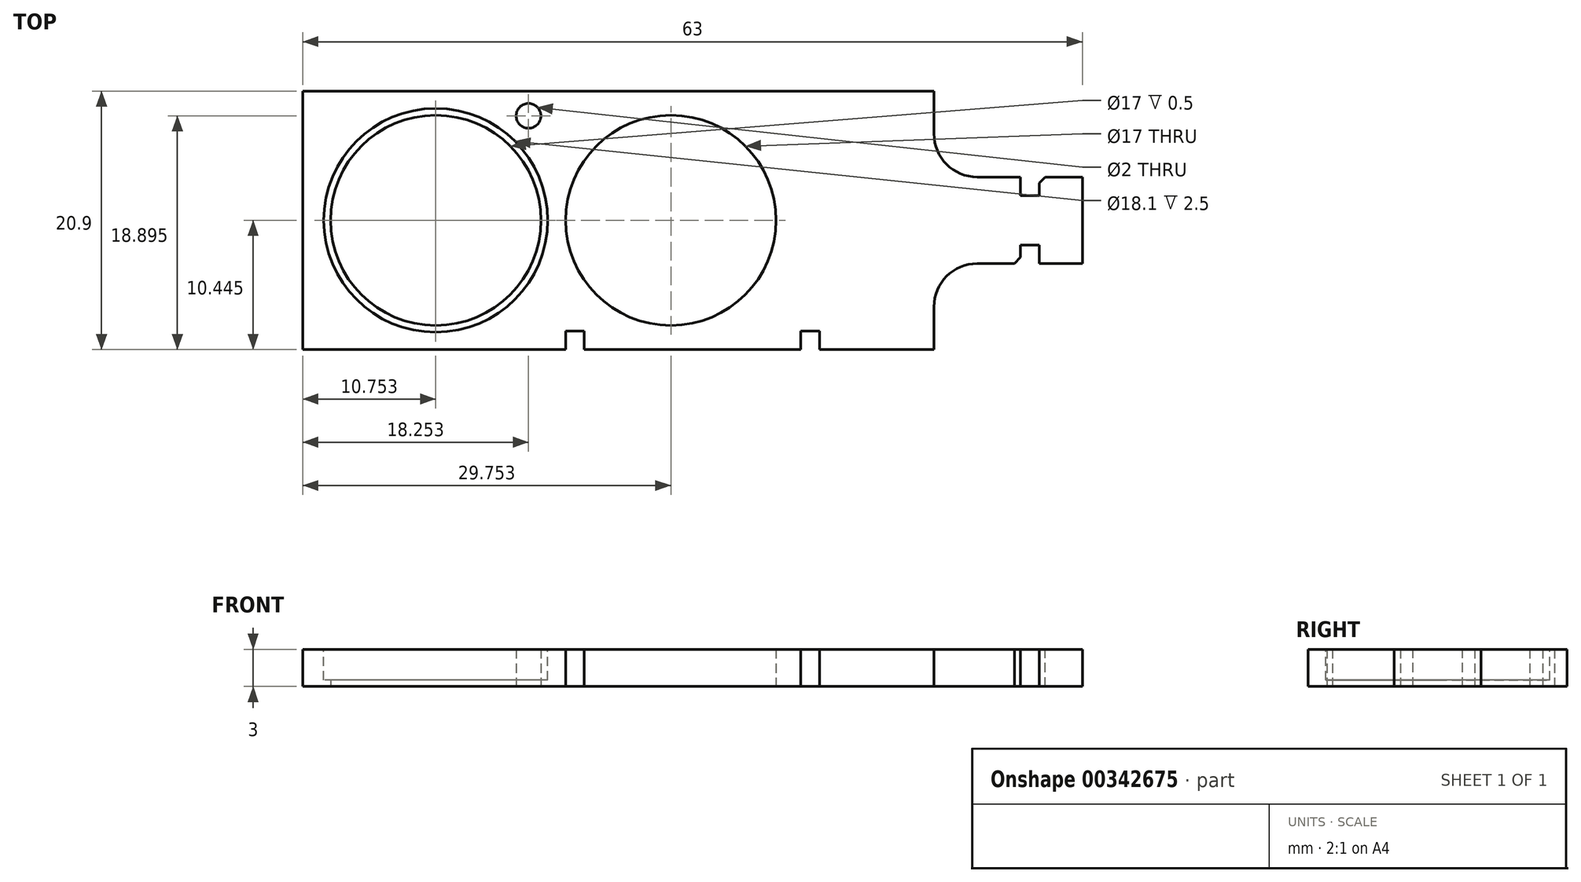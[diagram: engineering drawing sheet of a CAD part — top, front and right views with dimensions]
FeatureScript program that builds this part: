
annotation { "Feature Type Name" : "Feature", "Feature Type Description" : "" }
export const myFeature = defineFeature(function(context is Context, id is Id, definition is map)
    precondition{}
    {
        {
            var Q0;
            Q0=qCreatedBy(makeId("Top.planeOp"),FACE);
            var sketch = newSketch(context, id + "F0", { "sketchPlane" : qUnion([Q0])});
            skLineSegment(sketch, "E0", {"start": v(-30.6, 13.17) * mm, "end": v(20.4, 13.17) * mm});
            skLineSegment(sketch, "E1", {"start": v(20.4, 13.17) * mm, "end": v(20.4, 9.72) * mm});
            skLineSegment(sketch, "E2", {"start": v(23.9, 6.22) * mm, "end": v(32.4, 6.22) * mm});
            skLineSegment(sketch, "E3", {"start": v(32.4, 6.22) * mm, "end": v(32.4, -0.78) * mm});
            skLineSegment(sketch, "E4", {"start": v(32.4, -0.78) * mm, "end": v(23.9, -0.78) * mm});
            skLineSegment(sketch, "E5", {"start": v(20.4, -4.28) * mm, "end": v(20.4, -7.73) * mm});
            skLineSegment(sketch, "E6", {"start": v(-30.6, -7.73) * mm, "end": v(-30.6, 13.17) * mm});
            skPoint(sketch, "E7.orphan", {"position": v(-29.62, 13.17) * mm});
            skPoint(sketch, "E8.visualSharp", {"position": v(20.4, -0.78) * mm});
            skArc(sketch, "E8.filletArc", {"start": v(23.9, -0.78) * mm, "mid": v(21.42, -1.81) * mm, "end": v(20.4, -4.28) * mm});
            skPoint(sketch, "E9.visualSharp", {"position": v(20.4, 6.22) * mm});
            skArc(sketch, "E9.filletArc", {"start": v(20.4, 9.72) * mm, "mid": v(21.42, 7.24) * mm, "end": v(23.9, 6.22) * mm});
            skCircle(sketch, "E10", {"center": v(-19.86, 2.72) * mm, "radius": 8.5 * mm});
            skCircle(sketch, "E11", {"center": v(-0.86, 2.72) * mm, "radius": 8.5 * mm});
            skCircle(sketch, "E12", {"center": v(-12.36, 11.17) * mm, "radius": 1 * mm});
            skLineSegment(sketch, "E13.bottom", {"start": v(-9.36, -6.23) * mm, "end": v(-7.86, -6.23) * mm});
            skLineSegment(sketch, "E13.left", {"start": v(-9.36, -6.23) * mm, "end": v(-9.36, -7.73) * mm});
            skLineSegment(sketch, "E13.right", {"start": v(-7.86, -6.23) * mm, "end": v(-7.86, -7.73) * mm});
            skLineSegment(sketch, "E14.bottom", {"start": v(9.64, -6.23) * mm, "end": v(11.14, -6.23) * mm});
            skLineSegment(sketch, "E14.left", {"start": v(9.64, -6.23) * mm, "end": v(9.64, -7.73) * mm});
            skLineSegment(sketch, "E14.right", {"start": v(11.14, -6.23) * mm, "end": v(11.14, -7.73) * mm});
            skPoint(sketch, "E15", {"position": v(-8.6, -6.23) * mm});
            skPoint(sketch, "E16", {"position": v(10.4, -6.23) * mm});
            skLineSegment(sketch, "E17.trimOffspring", {"start": v(-9.36, -7.73) * mm, "end": v(-30.6, -7.73) * mm});
            skLineSegment(sketch, "E18.trimOffspring", {"start": v(9.64, -7.73) * mm, "end": v(-7.86, -7.73) * mm});
            skLineSegment(sketch, "E19", {"start": v(11.14, -7.73) * mm, "end": v(20.4, -7.73) * mm});
            skSolve(sketch);
        }
        {
            var Q0;
            Q0=qSketchRegion(id+"F0",true);
            extrude(context, id + "F1", {"entities" : qUnion([Q0]), "depth" : 3 * mm});
        }
        {
            var Q0;
            Q0=makeQuery(id+"F1.opExtrude","CAP_FACE",FACE,{"disambiguationData":[OSD([sQuery(id+"F0.wireOp",EDGE,"E0"),sQuery(id+"F0.wireOp",EDGE,"E1"),sQuery(id+"F0.wireOp",EDGE,"E2"),sQuery(id+"F0.wireOp",EDGE,"E3"),sQuery(id+"F0.wireOp",EDGE,"E4"),sQuery(id+"F0.wireOp",EDGE,"E5"),sQuery(id+"F0.wireOp",EDGE,"E6"),sQuery(id+"F0.wireOp",EDGE,"E8.filletArc"),sQuery(id+"F0.wireOp",EDGE,"E9.filletArc"),sQuery(id+"F0.wireOp",EDGE,"E10"),sQuery(id+"F0.wireOp",EDGE,"E11"),sQuery(id+"F0.wireOp",EDGE,"E12"),sQuery(id+"F0.wireOp",EDGE,"E13.bottom"),sQuery(id+"F0.wireOp",EDGE,"E13.left"),sQuery(id+"F0.wireOp",EDGE,"E13.right"),sQuery(id+"F0.wireOp",EDGE,"E14.bottom"),sQuery(id+"F0.wireOp",EDGE,"E14.left"),sQuery(id+"F0.wireOp",EDGE,"E14.right"),sQuery(id+"F0.wireOp",EDGE,"E17.trimOffspring"),sQuery(id+"F0.wireOp",EDGE,"E18.trimOffspring"),sQuery(id+"F0.wireOp",EDGE,"E19")])],"isStart":false});
            var sketch = newSketch(context, id + "F2", { "sketchPlane" : qUnion([Q0])});
            skCircle(sketch, "E20", {"center": v(-19.86, 2.72) * mm, "radius": 9.05 * mm});
            skSolve(sketch);
        }
        {
            var Q0;
            Q0=qSketchRegion(id+"F2",true);
            extrude(context, id + "F3", {"entities" : qUnion([Q0]), "operationType" : NewBodyOperationType.REMOVE, "oppositeDirection" : true, "depth" : 2.5 * mm});
        }
        {
            var Q0;
            Q0=makeQuery(id+"F1.opExtrude","CAP_FACE",FACE,{"disambiguationData":[OSD([sQuery(id+"F0.wireOp",EDGE,"E0"),sQuery(id+"F0.wireOp",EDGE,"E1"),sQuery(id+"F0.wireOp",EDGE,"E2"),sQuery(id+"F0.wireOp",EDGE,"E3"),sQuery(id+"F0.wireOp",EDGE,"E4"),sQuery(id+"F0.wireOp",EDGE,"E5"),sQuery(id+"F0.wireOp",EDGE,"E6"),sQuery(id+"F0.wireOp",EDGE,"E8.filletArc"),sQuery(id+"F0.wireOp",EDGE,"E9.filletArc"),sQuery(id+"F0.wireOp",EDGE,"E10"),sQuery(id+"F0.wireOp",EDGE,"E11"),sQuery(id+"F0.wireOp",EDGE,"E12"),sQuery(id+"F0.wireOp",EDGE,"E13.bottom"),sQuery(id+"F0.wireOp",EDGE,"E13.left"),sQuery(id+"F0.wireOp",EDGE,"E13.right"),sQuery(id+"F0.wireOp",EDGE,"E14.bottom"),sQuery(id+"F0.wireOp",EDGE,"E14.left"),sQuery(id+"F0.wireOp",EDGE,"E14.right"),sQuery(id+"F0.wireOp",EDGE,"E17.trimOffspring"),sQuery(id+"F0.wireOp",EDGE,"E18.trimOffspring"),sQuery(id+"F0.wireOp",EDGE,"E19")])],"isStart":false});
            var sketch = newSketch(context, id + "F4", { "sketchPlane" : qUnion([Q0])});
            skLineSegment(sketch, "E21.bottom", {"start": v(27.4, -0.78) * mm, "end": v(28.9, -0.78) * mm});
            skLineSegment(sketch, "E21.top", {"start": v(27.4, 0.72) * mm, "end": v(28.9, 0.72) * mm});
            skLineSegment(sketch, "E21.left", {"start": v(27.4, -0.78) * mm, "end": v(27.4, 0.72) * mm});
            skLineSegment(sketch, "E21.right", {"start": v(28.9, -0.78) * mm, "end": v(28.9, 0.72) * mm});
            skPoint(sketch, "E22", {"position": v(28.14, -0.78) * mm});
            skLineSegment(sketch, "E23.bottom", {"start": v(28.9, 6.22) * mm, "end": v(27.4, 6.22) * mm});
            skLineSegment(sketch, "E23.top", {"start": v(28.9, 4.72) * mm, "end": v(27.4, 4.72) * mm});
            skLineSegment(sketch, "E23.left", {"start": v(28.9, 6.22) * mm, "end": v(28.9, 4.72) * mm});
            skLineSegment(sketch, "E23.right", {"start": v(27.4, 6.22) * mm, "end": v(27.4, 4.72) * mm});
            skPoint(sketch, "E24", {"position": v(28.14, 6.22) * mm});
            skSolve(sketch);
        }
        {
            var Q0;
            Q0=qSketchRegion(id+"F4",true);
            extrude(context, id + "F5", {"entities" : qUnion([Q0]), "operationType" : NewBodyOperationType.REMOVE, "oppositeDirection" : true, "depth" : 3 * mm});
        }
        {
            var Q0;
            Q0=makeQuery(id+"F5.boolean.opBoolean","COPY",EDGE,{"derivedFrom":makeQuery(id+"F5.opExtrude","SWEPT_EDGE",EDGE,{"disambiguationData":[OSD([sQuery(id+"F0.wireOp",EDGE,"E4"),sQuery(id+"F4.wireOp",EDGE,"E21.bottom"),sQuery(id+"F4.wireOp",EDGE,"E21.left")])]})});
            var Q1;
            Q1=makeQuery(id+"F5.boolean.opBoolean","COPY",EDGE,{"derivedFrom":makeQuery(id+"F5.opExtrude","SWEPT_EDGE",EDGE,{"disambiguationData":[OSD([sQuery(id+"F0.wireOp",EDGE,"E4"),sQuery(id+"F4.wireOp",EDGE,"E21.bottom"),sQuery(id+"F4.wireOp",EDGE,"E21.right")])]})});
            var Q2;
            Q2=makeQuery(id+"F5.boolean.opBoolean","COPY",EDGE,{"derivedFrom":makeQuery(id+"F5.opExtrude","SWEPT_EDGE",EDGE,{"disambiguationData":[OSD([sQuery(id+"F0.wireOp",EDGE,"E2"),sQuery(id+"F4.wireOp",EDGE,"E23.bottom"),sQuery(id+"F4.wireOp",EDGE,"E23.left")])]})});
            var Q3;
            Q3=makeQuery(id+"F5.boolean.opBoolean","COPY",EDGE,{"derivedFrom":makeQuery(id+"F5.opExtrude","SWEPT_EDGE",EDGE,{"disambiguationData":[OSD([sQuery(id+"F0.wireOp",EDGE,"E2"),sQuery(id+"F4.wireOp",EDGE,"E23.bottom"),sQuery(id+"F4.wireOp",EDGE,"E23.right")])]})});
            chamfer(context, id + "F6", {"entities" : qUnion([Q0, Q1, Q2, Q3]), "width" : 0.5 * mm, "tangentPropagation" : true});
        }
    });
